# Revit family: RRHDWSTNTCP
name_source: partatom
category: Generic Models
revit_build: Autodesk Revit 2018 (Build: 20190510_1515(x64)
units: mm (PartAtom-declared; Revit-internal decimal feet)

## family parameters
Always vertical = No
Can host rebar = No
Cut with Voids When Loaded = No
Part Type = Normal
Room Calculation Point = No
Round Connector Dimension = Use Diameter
Shared = Yes
Work Plane-Based = Yes

## types (2) — shared parameters
Default Elevation = 48 "
Hardware Material = <By Category>
Patent Information = 10495237, 10,697,562, 10,844,978, 11,262,000

## per-type parameters (varying)
| type | Description | Sleeve Diameter | Sleeve Radius | Thread Diameter | Thread Radius |
| RRHDWSTNTCP3/8 | Turned rod coupler 3/8"-16 for Tented Rocket Rack | 0.386 " | 0.193 " | 0.313 " | 0.1565 " |
| RRHDWSTNTCP1/2 | Turned rod coupler 1/2-13 for Tented Rocket Rack | 0.506 " | 0.253 " | 0.422 " | 0.211 " |

note: column(s) folded — value = type name in every type: Catalog Number

## geometry (parser evidence)
native form markers: Sweep x3
no freeform markers — native parametric forms only
